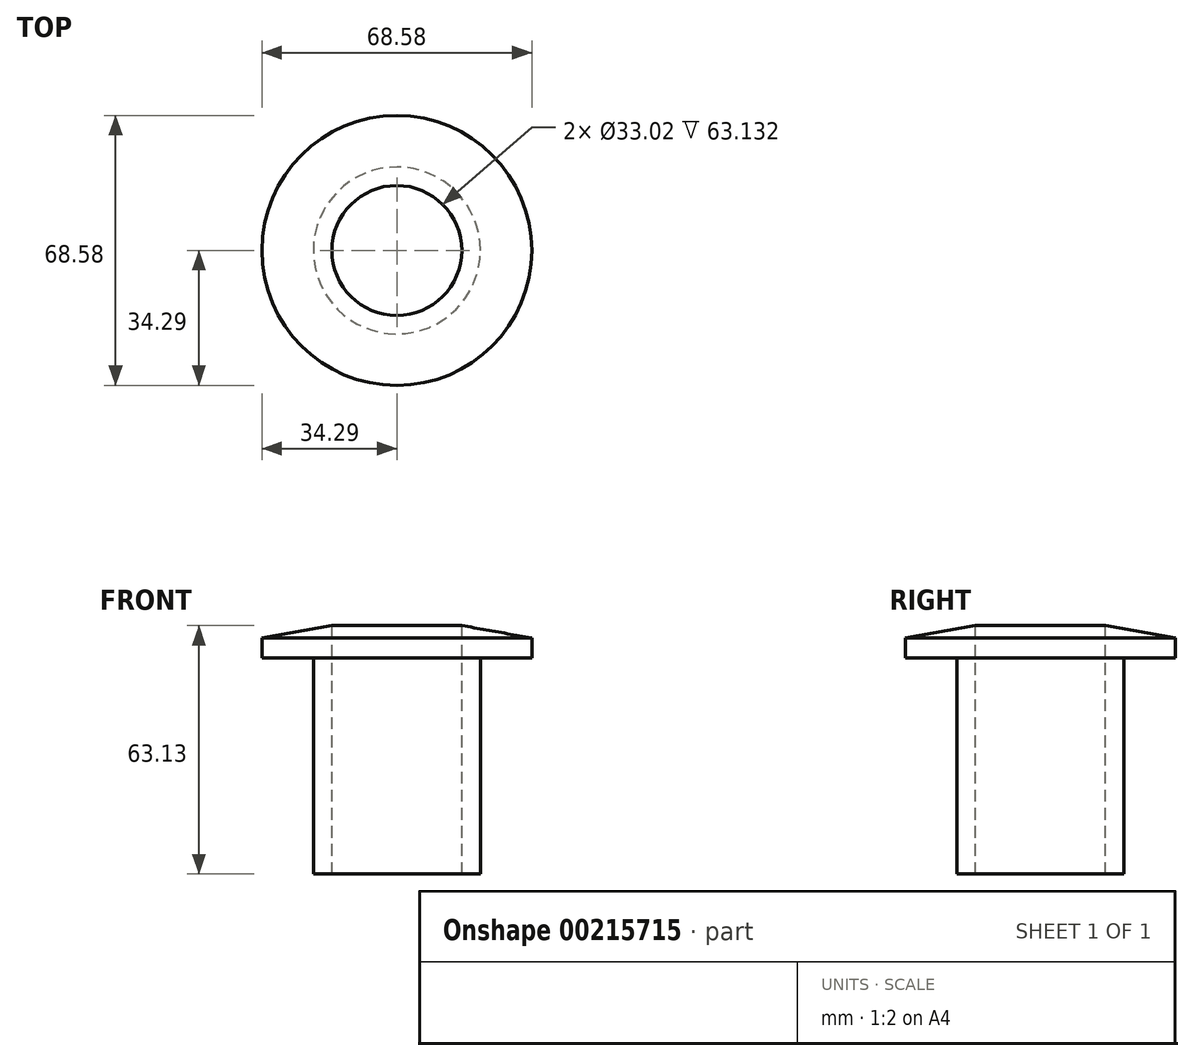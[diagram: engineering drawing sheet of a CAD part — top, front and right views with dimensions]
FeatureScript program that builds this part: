
annotation { "Feature Type Name" : "Feature", "Feature Type Description" : "" }
export const myFeature = defineFeature(function(context is Context, id is Id, definition is map)
    precondition{}
    {
        {
            var Q0;
            Q0=qCreatedBy(makeId("Front.planeOp"),FACE);
            var sketch = newSketch(context, id + "F0", { "sketchPlane" : qUnion([Q0])});
            skLineSegment(sketch, "E0", {"start": v(-21.2, 0) * mm, "end": v(-21.2, -54.86) * mm});
            skLineSegment(sketch, "E1", {"start": v(-21.2, -54.86) * mm, "end": v(21.2, -54.86) * mm});
            skLineSegment(sketch, "E2", {"start": v(21.2, -54.86) * mm, "end": v(21.2, 0) * mm});
            skLineSegment(sketch, "E3", {"start": v(21.2, 0) * mm, "end": v(34.3, 0) * mm});
            skLineSegment(sketch, "E4", {"start": v(34.3, 0) * mm, "end": v(34.3, 5.08) * mm});
            skLineSegment(sketch, "E5", {"start": v(34.3, 5.08) * mm, "end": v(16.51, 8.27) * mm});
            skLineSegment(sketch, "E6", {"start": v(16.51, 8.27) * mm, "end": v(-16.51, 8.27) * mm});
            skLineSegment(sketch, "E7", {"start": v(-16.51, 8.27) * mm, "end": v(-34.3, 5.08) * mm});
            skLineSegment(sketch, "E8", {"start": v(-34.3, 5.08) * mm, "end": v(-34.3, 0) * mm});
            skLineSegment(sketch, "E9", {"start": v(-34.3, 0) * mm, "end": v(-21.2, 0) * mm});
            skLineSegment(sketch, "E10", {"start": v(0, 8.27) * mm, "end": v(0, -54.86) * mm, "construction": true});
            skLineSegment(sketch, "E11", {"start": v(-16.51, 8.27) * mm, "end": v(-16.5, -54.86) * mm});
            skLineSegment(sketch, "E12", {"start": v(16.51, 8.27) * mm, "end": v(16.51, -54.86) * mm});
            skSolve(sketch);
        }
        {
            var Q0;
            {var subQ1=sQuery(id+"F0.wireOp",EDGE,"E0");Q0=makeQuery(id+"F0.imprint","IMPRINT",FACE,{"disambiguationData":[TD([[makeQuery(id+"F0.imprint","IMPRINT",EDGE,{"derivedFrom":subQ1}),1.0]])]});}
            var Q1;
            {var subQ0=sQuery(id+"F0.wireOp",EDGE,"E2");Q1=makeQuery(id+"F0.imprint","IMPRINT",FACE,{"disambiguationData":[TD([[makeQuery(id+"F0.imprint","IMPRINT",EDGE,{"derivedFrom":subQ0}),1.0]])]});}
            var Q2;
            Q2=sQuery(id+"F0.wireOp",EDGE,"E10");
            revolve(context, id + "F1", {"entities" : qUnion([Q0, Q1]), "axis" : qUnion([Q2]), "revolveType" : RevolveType.FULL});
        }
    });
